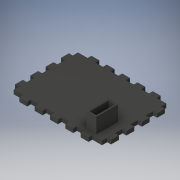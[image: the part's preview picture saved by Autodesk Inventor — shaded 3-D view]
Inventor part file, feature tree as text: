
AUTODESK INVENTOR PART (.ipt)
format: ipt  version: 2019 (Build 230136000, 136)  size: 234,496 bytes
history: native  units: mm
features: extrude x4, sketch x3
ambient origin geometry x8: Origin, YZ Plane, XZ Plane, XY Plane, X Axis, Y Axis, Z Axis, Center Point
bodies: Solid1 (feature_tree)
feature tree (7):
  extrude  "Extrusion1"  Depth=75.0mm
  extrude  "Extrusion3"  Depth=8.0mm
  extrude  "Extrusion4"  Depth=8.0mm
  extrude  "Extrusion5"  Depth=8.0mm
  sketch  "Sketch1"  dims[d0=100.0mm d1=75.0mm]
  sketch  "Sketch4"  dims[d2=4.0mm d3=0.0mm d9=8.0mm]
  sketch  "Sketch5"  dims[d11=4.0mm d12=8.0mm d13=8.0mm d14=8.0mm d15=8.0mm d16=8.0mm d17=4.0mm d18=8.0mm d19=4.0mm d20=0.0mm d22=4.0mm d23=7.0mm d24=20.0mm d25=14.0mm d26=8.0mm d27=10.0mm d28=0.0mm d29=1.5mm d30=16.0mm d31=0.0mm]
